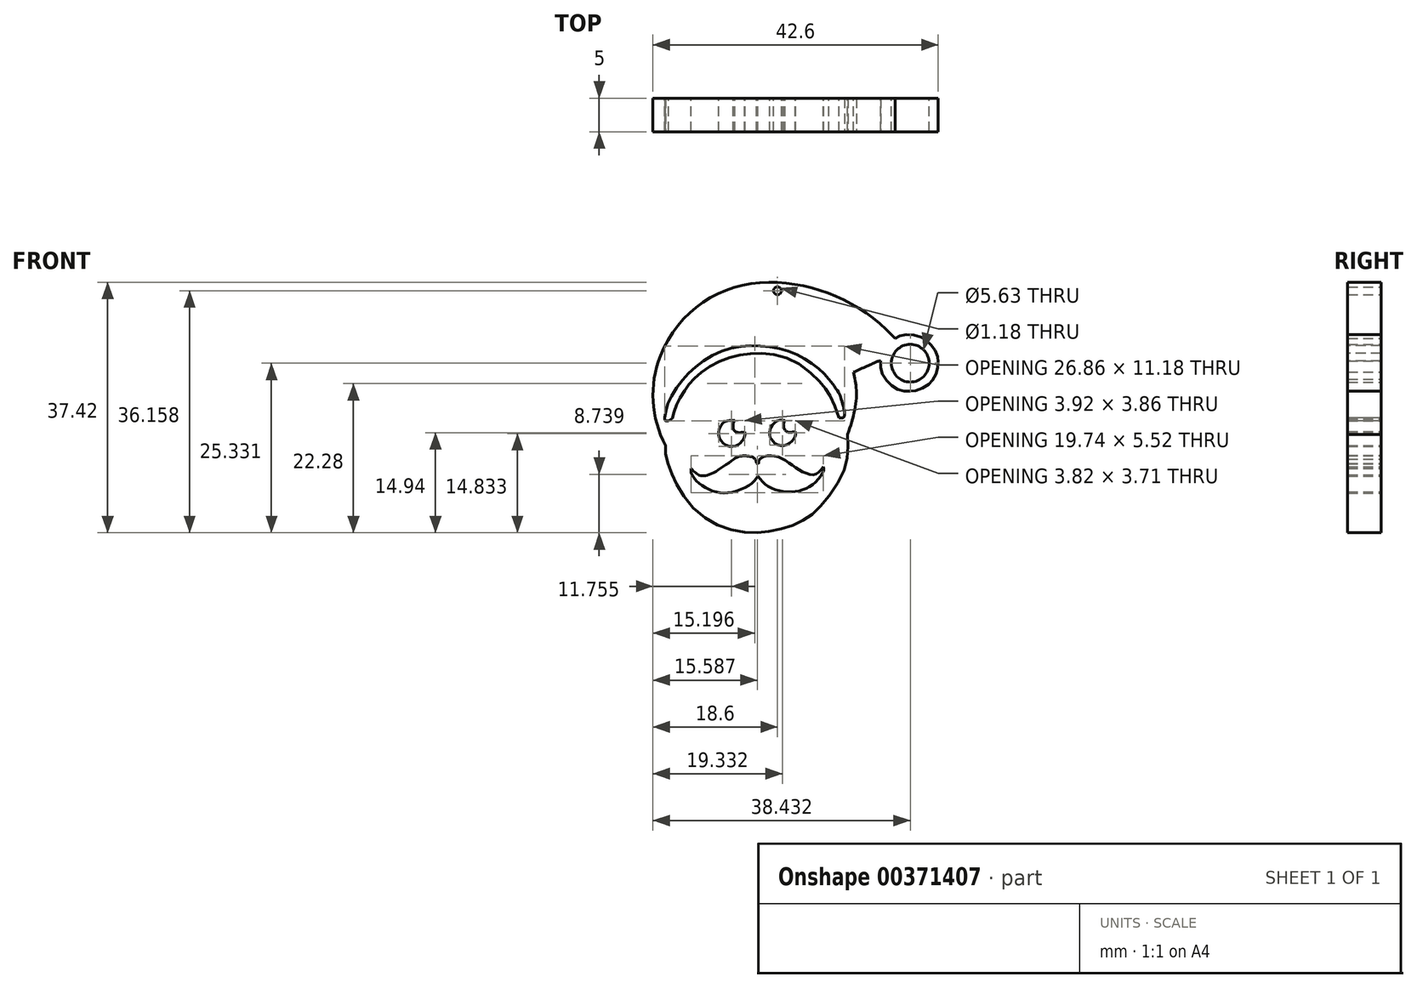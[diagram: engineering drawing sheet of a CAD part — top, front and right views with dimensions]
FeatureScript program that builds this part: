
annotation { "Feature Type Name" : "Feature", "Feature Type Description" : "" }
export const myFeature = defineFeature(function(context is Context, id is Id, definition is map)
    precondition{}
    {
        {
            var Q0;
            Q0=qCreatedBy(makeId("Front.planeOp"),FACE);
            var sketch = newSketch(context, id + "F0", { "sketchPlane" : qUnion([Q0])});
            skFitSpline(sketch, "E0", {"points": [v(19.13, 16.42) * mm, v(19.5, 16.02) * mm], "startDerivative": vector(0.38, -0.4) * mm, "endDerivative": vector(0.38, -0.4) * mm});
            skFitSpline(sketch, "E1", {"points": [v(19.5, 16.02) * mm, v(20.35, 16.42) * mm, v(21.83, 16.6) * mm, v(23.48, 16.15) * mm, v(24.47, 15.43) * mm, v(25.33, 14.48) * mm, v(25.9, 13.12) * mm, v(25.94, 12.3) * mm, v(25.76, 11.08) * mm, v(25.17, 9.86) * mm, v(24.33, 9) * mm, v(22.75, 8.26) * mm, v(21.82, 8.12) * mm, v(20.6, 8.19) * mm, v(19.38, 8.73) * mm, v(18.14, 9.86) * mm, v(17.4, 11.3) * mm, v(17.39, 12.63) * mm], "startDerivative": vector(15.63, 8.7) * mm, "endDerivative": vector(2.04, 22.53) * mm});
            skCircle(sketch, "E2", {"center": v(21.78, 12.31) * mm, "radius": 2.81 * mm});
            skPoint(sketch, "E2.first.point", {"position": v(21.48, 15.1) * mm});
            skPoint(sketch, "E2.second.point", {"position": v(24.6, 12.37) * mm});
            skPoint(sketch, "E2.third.point", {"position": v(20.26, 9.95) * mm});
            skFitSpline(sketch, "E3", {"points": [v(17.39, 12.63) * mm, v(17.12, 12.63) * mm, v(16.26, 12.3) * mm, v(13.28, 10.97) * mm], "startDerivative": vector(-1.55, 0.18) * mm, "endDerivative": vector(-6.13, -2.72) * mm});
            skFitSpline(sketch, "E4", {"points": [v(12.44, 1.67) * mm, v(12.44, -1.42) * mm, v(11.49, -4.6) * mm, v(8.8, -8.6) * mm, v(6.7, -10.56) * mm, v(4.36, -11.85) * mm, v(1.25, -12.74) * mm, v(-1.82, -13.02) * mm, v(-5.7, -12.36) * mm, v(-9.65, -10.2) * mm, v(-12.72, -6.5) * mm, v(-14, -3.81) * mm, v(-14.7, -1.58) * mm, v(-14.78, 0) * mm], "startDerivative": vector(2.13, -41.72) * mm, "endDerivative": vector(0.68, 28.41) * mm});
            skFitSpline(sketch, "E5", {"points": [v(-14.35, 3.71) * mm, v(-13.81, 4.01) * mm, v(-13.46, 5.13) * mm, v(-12.9, 6.63) * mm, v(-11.89, 8.22) * mm, v(-10.9, 9.6) * mm, v(-9.25, 11.09) * mm, v(-6.41, 12.74) * mm, v(-3.37, 13.6) * mm, v(0, 13.75) * mm, v(4.64, 12.5) * mm, v(8.4, 9.36) * mm, v(9.69, 7.7) * mm, v(11.16, 4.14) * mm], "startDerivative": vector(15.64, 5.17) * mm, "endDerivative": vector(15.45, -41.88) * mm});
            skFitSpline(sketch, "E6", {"points": [v(11.16, 4.14) * mm, v(11.59, 4.14) * mm, v(11.97, 4.47) * mm, v(11.61, 6.47) * mm, v(11.16, 7.77) * mm, v(9.64, 9.9) * mm], "startDerivative": vector(3.63, -0.39) * mm, "endDerivative": vector(-6.24, 7.96) * mm});
            skFitSpline(sketch, "E7", {"points": [v(9.64, 9.9) * mm, v(7.91, 11.67) * mm, v(5.28, 13.37) * mm, v(2, 14.54) * mm, v(-2.13, 14.92) * mm, v(-6.06, 14.2) * mm, v(-9.91, 12.08) * mm, v(-12.57, 9.36) * mm, v(-14.45, 6.2) * mm, v(-14.88, 4.2) * mm], "startDerivative": vector(-16.8, 19.21) * mm, "endDerivative": vector(-2.69, -22.11) * mm});
            skFitSpline(sketch, "E8", {"points": [v(-14.88, 4.2) * mm, v(-14.8, 3.71) * mm, v(-14.35, 3.71) * mm], "startDerivative": vector(-0.05, -1.19) * mm, "endDerivative": vector(1.12, 0.23) * mm});
            skFitSpline(sketch, "E9", {"points": [v(-4.42, 3.74) * mm, v(-4.64, 3.38) * mm, v(-4.7, 2.8) * mm, v(-4.46, 2.18) * mm, v(-3.89, 1.95) * mm, v(-2.94, 2.02) * mm], "startDerivative": vector(-1.52, -2.03) * mm, "endDerivative": vector(4.06, 0.6) * mm});
            skFitSpline(sketch, "E10", {"points": [v(3.09, 3.78) * mm, v(2.9, 3.45) * mm, v(2.85, 2.95) * mm, v(3.02, 2.45) * mm, v(3.32, 2.1) * mm, v(3.77, 1.98) * mm, v(4.6, 2.1) * mm], "startDerivative": vector(-1.44, -2.1) * mm, "endDerivative": vector(4.17, 0.76) * mm});
            skFitSpline(sketch, "E11", {"points": [v(4.6, 2.1) * mm, v(4.6, 1.41) * mm, v(3.95, 0.53) * mm, v(2.9, 0) * mm, v(1.69, 0.26) * mm, v(1.08, 0.94) * mm, v(0.8, 1.48) * mm, v(0.86, 2.45) * mm, v(1.17, 3.08) * mm, v(2.17, 3.81) * mm, v(3.09, 3.78) * mm], "startDerivative": vector(1.26, -7.85) * mm, "endDerivative": vector(9.04, -2.05) * mm});
            skFitSpline(sketch, "E12", {"points": [v(-10.93, -3.43) * mm, v(-9.94, -4.3) * mm, v(-8.55, -4.43) * mm, v(-4.53, -2.01) * mm], "startDerivative": vector(3.63, -3.95) * mm, "endDerivative": vector(9.25, 6.64) * mm});
            skFitSpline(sketch, "E13", {"points": [v(-4.53, -2.01) * mm, v(-3.72, -1.6) * mm, v(-2.2, -1.6) * mm, v(-1.4, -2.01) * mm, v(-1.16, -2.68) * mm], "startDerivative": vector(2.94, 2.04) * mm, "endDerivative": vector(0.66, -3.43) * mm});
            skFitSpline(sketch, "E14", {"points": [v(-1.16, -2.68) * mm, v(-0.93, -2.68) * mm, v(-0.8, -2.2) * mm, v(0.34, -1.53) * mm, v(2.24, -1.76) * mm, v(4.1, -2.9) * mm, v(6.06, -4.08) * mm, v(7.62, -4.3) * mm, v(8.8, -3.14) * mm], "startDerivative": vector(5.37, -1.35) * mm, "endDerivative": vector(7.77, 10.57) * mm});
            skFitSpline(sketch, "E15", {"points": [v(8.8, -3.14) * mm, v(8.8, -3.8) * mm, v(7.55, -5.55) * mm, v(5.5, -6.67) * mm, v(2.96, -6.87) * mm, v(0.52, -6.07) * mm, v(-0.96, -4.58) * mm], "startDerivative": vector(1.23, -6.13) * mm, "endDerivative": vector(-7.68, 9.51) * mm});
            skFitSpline(sketch, "E16", {"points": [v(-0.96, -4.58) * mm, v(-2.06, -5.78) * mm, v(-5.07, -7.02) * mm, v(-7.61, -6.82) * mm, v(-9.75, -5.65) * mm, v(-10.9, -4.16) * mm, v(-10.93, -3.43) * mm], "startDerivative": vector(-5.7, -8.1) * mm, "endDerivative": vector(0.83, 6.75) * mm});
            skCircle(sketch, "E17", {"center": v(1.95, 23.14) * mm, "radius": 0.59 * mm});
            skArc(sketch, "E18", {"start": v(0.64, 24.4) * mm, "mid": v(-9.16, 21.41) * mm, "end": v(-15.54, 13.4) * mm});
            skArc(sketch, "E19", {"start": v(0.64, 24.4) * mm, "mid": v(10.7, 22.3) * mm, "end": v(19.13, 16.42) * mm});
            skArc(sketch, "E20", {"start": v(-15.54, 13.4) * mm, "mid": v(-16.62, 6.62) * mm, "end": v(-14.78, 0) * mm});
            skFitSpline(sketch, "E21", {"points": [v(13.28, 10.97) * mm, v(13.67, 8.88) * mm, v(13.57, 5.82) * mm, v(12.44, 1.67) * mm], "startDerivative": vector(1.68, -7.24) * mm, "endDerivative": vector(-3.5, -10.83) * mm});
            skFitSpline(sketch, "E22", {"points": [v(-2.94, 2.02) * mm, v(-2.94, 1.4) * mm, v(-3.45, 0.57) * mm, v(-4.23, 0) * mm, v(-5.6, 0) * mm, v(-6.62, 0.96) * mm, v(-6.83, 2.18) * mm, v(-6.16, 3.37) * mm, v(-5.39, 3.74) * mm, v(-4.42, 3.74) * mm], "startDerivative": vector(1.06, -7.05) * mm, "endDerivative": vector(9.44, -0.65) * mm});
            skSolve(sketch);
        }
        {
            var Q0;
            Q0 = qSketchRegion(id + "F0", true);
            var Q1;
            Q1=makeQuery(id+"F0.imprint","IMPRINT",FACE,{"disambiguationData":[TD([[makeQuery(id+"F0.imprint","IMPRINT",EDGE,{"derivedFrom":sQuery(id+"F0.wireOp",EDGE,"6d281c1b-e7ef-466d-84dc-30a1bc8d22e4")}),-1.0]])]});
            extrude(context, id + "F1", {"entities" : qUnion([Q0, Q1]), "depth" : 5 * mm});
        }
    });
